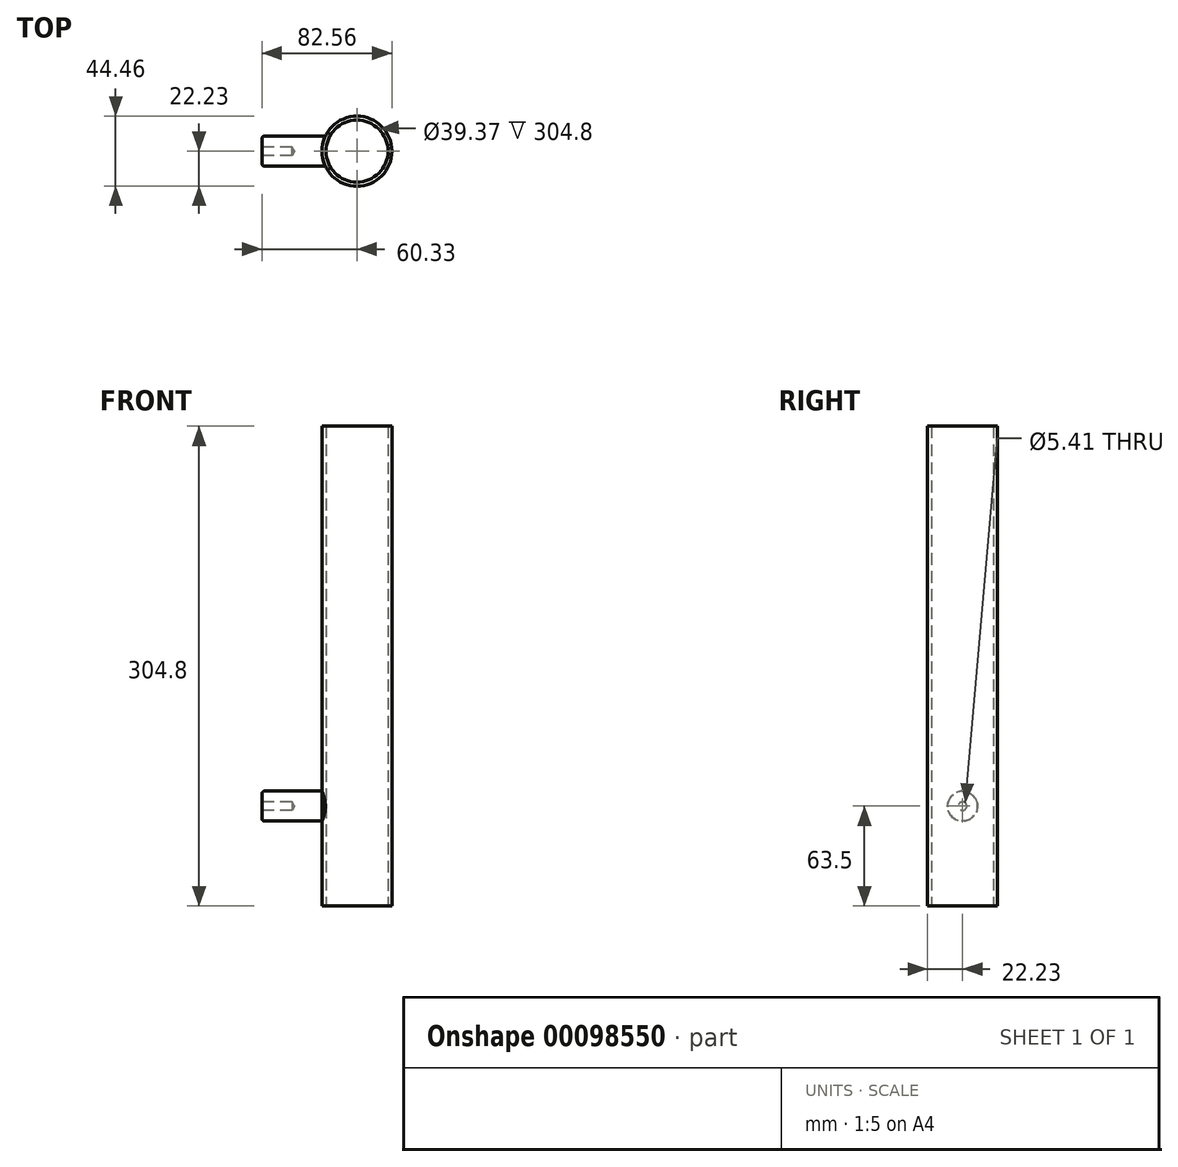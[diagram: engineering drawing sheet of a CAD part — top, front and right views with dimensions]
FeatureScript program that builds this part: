
annotation { "Feature Type Name" : "Feature", "Feature Type Description" : "" }
export const myFeature = defineFeature(function(context is Context, id is Id, definition is map)
    precondition{}
    {
        {
            var Q0;
            Q0=qCreatedBy(makeId("Top.planeOp"),FACE);
            var sketch = newSketch(context, id + "F0", { "sketchPlane" : qUnion([Q0])});
            skCircle(sketch, "E0", {"center": v(0, 0) * mm, "radius": 19.69 * mm});
            skCircle(sketch, "E1", {"center": v(0, 0) * mm, "radius": 22.23 * mm});
            skSolve(sketch);
        }
        {
            var Q0;
            Q0=qSketchRegion(id+"F0",true);
            extrude(context, id + "F1", {"entities" : qUnion([Q0]), "depth" : 304.8 * mm});
        }
        {
            var Q0;
            Q0=qCreatedBy(makeId("Front.planeOp"),FACE);
            var sketch = newSketch(context, id + "F2", { "sketchPlane" : qUnion([Q0])});
            skLineSegment(sketch, "E2", {"start": v(0, 0) * mm, "end": v(0, 63.5) * mm});
            skLineSegment(sketch, "E3", {"start": v(0, 63.5) * mm, "end": v(-60.33, 63.5) * mm});
            skSolve(sketch);
        }
        {
            var Q0;
            Q0=sQuery(id+"F2.wireOp",VERTEX,"E3.end");
            var Q1;
            Q1=sQuery(id+"F2.wireOp",EDGE,"E3");
            cPlane(context, id + "F3", {"entities" : qUnion([Q0, Q1]), "cplaneType" : CPlaneType.LINE_POINT, "offset" : 152.4 * mm, "width" : 152.4 * mm, "height" : 152.4 * mm});
        }
        {
            var Q0;
            Q0=qCreatedBy(id+"F3.planeOp",FACE);
            var sketch = newSketch(context, id + "F4", { "sketchPlane" : qUnion([Q0])});
            skCircle(sketch, "E4", {"center": v(0, 63.5) * mm, "radius": 9.53 * mm});
            skSolve(sketch);
        }
        {
            var Q0;
            Q0=makeQuery(id+"F4.imprint","IMPRINT",FACE,{"disambiguationData":[TD([[makeQuery(id+"F4.imprint","IMPRINT",EDGE,{"derivedFrom":sQuery(id+"F4.wireOp",EDGE,"E4")}),1.0]])]});
            extrude(context, id + "F5", {"entities" : qUnion([Q0]), "endBound" : BoundingType.UP_TO_NEXT, "oppositeDirection" : true, "depth" : 25.4 * mm});
        }
        {
            var Q0;
            Q0=makeQuery(id+"F5.opExtrude","CAP_FACE",FACE,{"disambiguationData":[OSD([sQuery(id+"F4.wireOp",EDGE,"E4")])],"isStart":true});
            var sketch = newSketch(context, id + "F6", { "sketchPlane" : qUnion([Q0])});
            skPoint(sketch, "E5", {"position": v(0, 63.5) * mm});
            skSolve(sketch);
        }
        {
            var Q0;
            Q0=sQuery(id+"F6.wireOp",VERTEX,"E5");
            var Q1;
            Q1=makeQuery(id+"F5.opExtrude","SWEPT_BODY",BODY,{"disambiguationData":[OSD([sQuery(id+"F4.wireOp",EDGE,"E4")])]});
            hole(context, id + "F7", {"style" : HoleStyle.SIMPLE, "endStyle" : HoleEndStyle.BLIND, "standardTappedOrClearance" : lookupTablePath({ "standard" : "ANSI", "engagement" : "75%", "pitch" : "28 tpi", "size" : "1/4", "type" : "Tapped" }), "standardBlindInLast" : lookupTablePath({ "standard" : "ANSI", "engagement" : "75%", "pitch" : "28 tpi", "size" : "1/4", "type" : "Tapped" }), "holeDiameter" : 5.4 * mm, "holeDepth" : 19.05 * mm, "locations" : qUnion([Q0]), "scope" : qUnion([Q1]), "majorDiameter" : 6.35 * mm});
        }
        {
            var Q0;
            Q0=makeQuery(id+"F5.opExtrude","CAP_EDGE",EDGE,{"disambiguationData":[OSD([sQuery(id+"F4.wireOp",EDGE,"E4")])],"isStart":true});
            fillet(context, id + "F8", {"entities" : qUnion([Q0]), "radius" : 1.59 * mm, "tangentPropagation" : true, "allowEdgeOverflow" : false});
        }
    });
